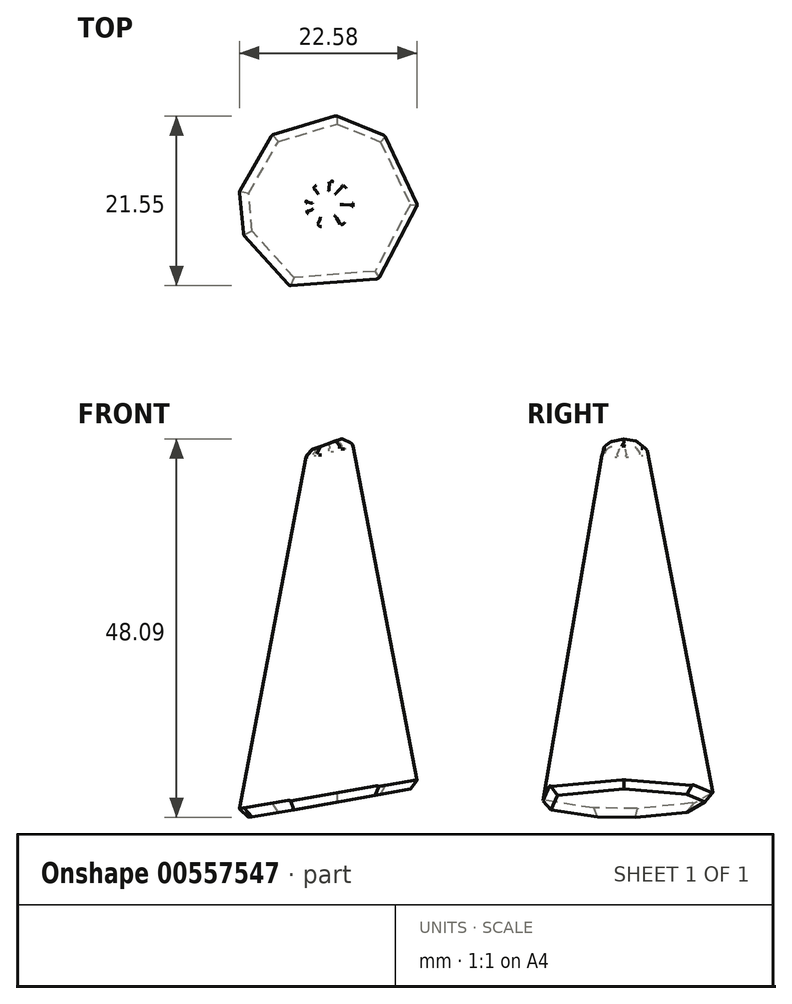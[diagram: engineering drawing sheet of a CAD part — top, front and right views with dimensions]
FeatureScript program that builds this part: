
annotation { "Feature Type Name" : "Feature", "Feature Type Description" : "" }
export const myFeature = defineFeature(function(context is Context, id is Id, definition is map)
    precondition{}
    {
        {
            var Q0;
            Q0=qCreatedBy(makeId("Top.planeOp"),FACE);
            cPlane(context, id + "F0", {"entities" : qUnion([Q0]), "cplaneType" : CPlaneType.OFFSET, "offset" : 60 * mm, "width" : 150 * mm, "height" : 150 * mm});
        }
        {
            var Q0;
            Q0=qCreatedBy(makeId("Top.planeOp"),FACE);
            var sketch = newSketch(context, id + "F1", { "sketchPlane" : qUnion([Q0])});
            skCircle(sketch, "E0", {"center": v(0, 0) * mm, "radius": 12 * mm, "construction": true});
            skLineSegment(sketch, "E1", {"start": v(-11.88, 1.7) * mm, "end": v(-7.77, 9.15) * mm});
            skLineSegment(sketch, "E2", {"start": v(-7.77, 9.15) * mm, "end": v(0.67, 11.98) * mm});
            skLineSegment(sketch, "E3", {"start": v(0.67, 11.98) * mm, "end": v(7.4, 9.44) * mm});
            skLineSegment(sketch, "E4", {"start": v(7.4, 9.44) * mm, "end": v(12, 0) * mm});
            skLineSegment(sketch, "E5", {"start": v(12, 0) * mm, "end": v(6.49, -10.1) * mm});
            skLineSegment(sketch, "E6", {"start": v(6.49, -10.1) * mm, "end": v(-5.5, -10.67) * mm});
            skLineSegment(sketch, "E7", {"start": v(-5.5, -10.67) * mm, "end": v(-11.37, -3.85) * mm});
            skLineSegment(sketch, "E8", {"start": v(-11.37, -3.85) * mm, "end": v(-11.88, 1.7) * mm});
            skSolve(sketch);
        }
        {
            var Q0;
            Q0=qCreatedBy(id+"F0.planeOp",FACE);
            var sketch = newSketch(context, id + "F2", { "sketchPlane" : qUnion([Q0])});
            skCircle(sketch, "E9", {"center": v(0, 0) * mm, "radius": 0.5 * mm, "construction": true});
            skPoint(sketch, "E10.0", {"position": v(-7.77, 9.15) * mm});
            skPoint(sketch, "E11.0", {"position": v(0.67, 11.98) * mm});
            skPoint(sketch, "E12.0", {"position": v(7.4, 9.44) * mm});
            skPoint(sketch, "E13.0", {"position": v(12, 0) * mm});
            skPoint(sketch, "E14.0", {"position": v(6.49, -10.1) * mm});
            skPoint(sketch, "E15.0", {"position": v(-5.5, -10.67) * mm});
            skPoint(sketch, "E16.0", {"position": v(-11.37, -3.85) * mm});
            skPoint(sketch, "E17.0", {"position": v(-11.88, 1.7) * mm});
            skLineSegment(sketch, "E18", {"start": v(0, 0) * mm, "end": v(-7.77, 9.15) * mm, "construction": true});
            skLineSegment(sketch, "E19", {"start": v(0, 0) * mm, "end": v(0.67, 11.98) * mm, "construction": true});
            skLineSegment(sketch, "E20", {"start": v(0, 0) * mm, "end": v(7.4, 9.44) * mm, "construction": true});
            skLineSegment(sketch, "E21", {"start": v(0, 0) * mm, "end": v(12, 0) * mm, "construction": true});
            skLineSegment(sketch, "E22", {"start": v(6.49, -10.1) * mm, "end": v(0, 0) * mm, "construction": true});
            skLineSegment(sketch, "E23", {"start": v(-5.5, -10.67) * mm, "end": v(0, 0) * mm, "construction": true});
            skLineSegment(sketch, "E24", {"start": v(-11.37, -3.85) * mm, "end": v(0, 0) * mm, "construction": true});
            skLineSegment(sketch, "E25", {"start": v(-11.88, 1.7) * mm, "end": v(0, 0) * mm, "construction": true});
            skLineSegment(sketch, "E26", {"start": v(0.03, 0.5) * mm, "end": v(0.3, 0.4) * mm});
            skLineSegment(sketch, "E27", {"start": v(0.3, 0.4) * mm, "end": v(0.5, 0) * mm});
            skLineSegment(sketch, "E28", {"start": v(0.5, 0) * mm, "end": v(0.27, -0.42) * mm});
            skLineSegment(sketch, "E29", {"start": v(0.27, -0.42) * mm, "end": v(-0.23, -0.44) * mm});
            skLineSegment(sketch, "E30", {"start": v(-0.23, -0.44) * mm, "end": v(-0.47, -0.16) * mm});
            skLineSegment(sketch, "E31", {"start": v(-0.47, -0.16) * mm, "end": v(-0.5, 0.07) * mm});
            skLineSegment(sketch, "E32", {"start": v(-0.5, 0.07) * mm, "end": v(-0.32, 0.38) * mm});
            skLineSegment(sketch, "E33", {"start": v(-0.32, 0.38) * mm, "end": v(0.03, 0.5) * mm});
            skSolve(sketch);
        }
        {
            var Q0;
            Q0=qSketchRegion(id+"F2",true);
            var Q1;
            Q1=qSketchRegion(id+"F1",true);
            loft(context, id + "F3", {"sheetProfilesArray" : [{ "sheetProfileEntities" : qUnion([Q0]) }, { "sheetProfileEntities" : qUnion([Q1]) }]});
        }
        {
            var Q0;
            Q0=qCreatedBy(makeId("Front.planeOp"),FACE);
            var sketch = newSketch(context, id + "F4", { "sketchPlane" : qUnion([Q0])});
            skLineSegment(sketch, "E34", {"start": v(-11.88, 0) * mm, "end": v(12, 4.21) * mm});
            skLineSegment(sketch, "E35", {"start": v(12, 4.21) * mm, "end": v(12, 0) * mm});
            skLineSegment(sketch, "E36", {"start": v(12, 0) * mm, "end": v(-11.88, 0) * mm});
            skSolve(sketch);
        }
        {
            var Q0;
            Q0=qSketchRegion(id+"F4",true);
            extrude(context, id + "F5", {"entities" : qUnion([Q0]), "operationType" : NewBodyOperationType.REMOVE, "endBound" : BoundingType.THROUGH_ALL, "oppositeDirection" : true, "depth" : 25 * mm, "offsetDistance" : 25 * mm, "hasSecondDirection" : true, "secondDirectionBound" : BoundingType.THROUGH_ALL, "secondDirectionOppositeDirection" : false, "secondDirectionDepth" : 25 * mm});
        }
        {
            var Q0;
            Q0=qCreatedBy(makeId("Front.planeOp"),FACE);
            var sketch = newSketch(context, id + "F6", { "sketchPlane" : qUnion([Q0])});
            skLineSegment(sketch, "E37", {"start": v(-3, 46.8) * mm, "end": v(2.64, 48.85) * mm});
            skLineSegment(sketch, "E38", {"start": v(2.64, 48.85) * mm, "end": v(0.5, 60) * mm});
            skLineSegment(sketch, "E39", {"start": v(0.5, 60) * mm, "end": v(-0.5, 60) * mm});
            skLineSegment(sketch, "E40", {"start": v(-0.5, 60) * mm, "end": v(-3, 46.8) * mm});
            skSolve(sketch);
        }
        {
            var Q0;
            Q0 = qSketchRegion(id + "F6", true);
            extrude(context, id + "F7", {"entities" : qUnion([Q0]), "operationType" : NewBodyOperationType.REMOVE, "endBound" : BoundingType.THROUGH_ALL, "oppositeDirection" : true, "depth" : 25 * mm, "offsetDistance" : 25 * mm, "hasSecondDirection" : true, "secondDirectionBound" : BoundingType.THROUGH_ALL, "secondDirectionOppositeDirection" : false, "secondDirectionDepth" : 25 * mm});
        }
        {
            var Q0;
            Q0=makeQuery(id+"F5.boolean.opBoolean","INTERSECT",EDGE,{"derivedFrom":[makeQuery(id+"F3.opLoft","SWEPT_FACE",FACE,{"disambiguationData":[OSD([sQuery(id+"F1.wireOp",EDGE,"E5"),sQuery(id+"F1.wireOp",EDGE,"E6"),sQuery(id+"F1.wireOp",EDGE,"E7"),sQuery(id+"F2.wireOp",EDGE,"E28"),sQuery(id+"F2.wireOp",EDGE,"E29"),sQuery(id+"F2.wireOp",EDGE,"E30")])]}),makeQuery(id+"F5.opExtrude","SWEPT_FACE",FACE,{"disambiguationData":[OSD([sQuery(id+"F4.wireOp",EDGE,"E34")])]})]});
            var Q1;
            Q1=makeQuery(id+"F5.boolean.opBoolean","INTERSECT",EDGE,{"derivedFrom":[makeQuery(id+"F3.opLoft","SWEPT_FACE",FACE,{"disambiguationData":[OSD([sQuery(id+"F1.wireOp",EDGE,"E4"),sQuery(id+"F1.wireOp",EDGE,"E5"),sQuery(id+"F1.wireOp",EDGE,"E6"),sQuery(id+"F2.wireOp",EDGE,"E27"),sQuery(id+"F2.wireOp",EDGE,"E28"),sQuery(id+"F2.wireOp",EDGE,"E29")])]}),makeQuery(id+"F5.opExtrude","SWEPT_FACE",FACE,{"disambiguationData":[OSD([sQuery(id+"F4.wireOp",EDGE,"E34")])]})]});
            var Q2;
            Q2=makeQuery(id+"F5.boolean.opBoolean","INTERSECT",EDGE,{"derivedFrom":[makeQuery(id+"F3.opLoft","SWEPT_FACE",FACE,{"disambiguationData":[OSD([sQuery(id+"F1.wireOp",EDGE,"E6"),sQuery(id+"F1.wireOp",EDGE,"E7"),sQuery(id+"F1.wireOp",EDGE,"E8"),sQuery(id+"F2.wireOp",EDGE,"E29"),sQuery(id+"F2.wireOp",EDGE,"E30"),sQuery(id+"F2.wireOp",EDGE,"E31")])]}),makeQuery(id+"F5.opExtrude","SWEPT_FACE",FACE,{"disambiguationData":[OSD([sQuery(id+"F4.wireOp",EDGE,"E34")])]})]});
            var Q3;
            Q3=makeQuery(id+"F5.boolean.opBoolean","INTERSECT",EDGE,{"derivedFrom":[makeQuery(id+"F3.opLoft","SWEPT_FACE",FACE,{"disambiguationData":[OSD([sQuery(id+"F1.wireOp",EDGE,"E1"),sQuery(id+"F1.wireOp",EDGE,"E7"),sQuery(id+"F1.wireOp",EDGE,"E8"),sQuery(id+"F2.wireOp",EDGE,"E30"),sQuery(id+"F2.wireOp",EDGE,"E31"),sQuery(id+"F2.wireOp",EDGE,"E32")])]}),makeQuery(id+"F5.opExtrude","SWEPT_FACE",FACE,{"disambiguationData":[OSD([sQuery(id+"F4.wireOp",EDGE,"E34")])]})]});
            var Q4;
            Q4=makeQuery(id+"F5.boolean.opBoolean","INTERSECT",EDGE,{"derivedFrom":[makeQuery(id+"F3.opLoft","SWEPT_FACE",FACE,{"disambiguationData":[OSD([sQuery(id+"F1.wireOp",EDGE,"E3"),sQuery(id+"F1.wireOp",EDGE,"E4"),sQuery(id+"F1.wireOp",EDGE,"E5"),sQuery(id+"F2.wireOp",EDGE,"E26"),sQuery(id+"F2.wireOp",EDGE,"E27"),sQuery(id+"F2.wireOp",EDGE,"E28")])]}),makeQuery(id+"F5.opExtrude","SWEPT_FACE",FACE,{"disambiguationData":[OSD([sQuery(id+"F4.wireOp",EDGE,"E34")])]})]});
            var Q5;
            Q5=makeQuery(id+"F5.boolean.opBoolean","INTERSECT",EDGE,{"derivedFrom":[makeQuery(id+"F3.opLoft","SWEPT_FACE",FACE,{"disambiguationData":[OSD([sQuery(id+"F1.wireOp",EDGE,"E2"),sQuery(id+"F1.wireOp",EDGE,"E3"),sQuery(id+"F1.wireOp",EDGE,"E4"),sQuery(id+"F2.wireOp",EDGE,"E26"),sQuery(id+"F2.wireOp",EDGE,"E27"),sQuery(id+"F2.wireOp",EDGE,"E33")])]}),makeQuery(id+"F5.opExtrude","SWEPT_FACE",FACE,{"disambiguationData":[OSD([sQuery(id+"F4.wireOp",EDGE,"E34")])]})]});
            var Q6;
            Q6=makeQuery(id+"F5.boolean.opBoolean","INTERSECT",EDGE,{"derivedFrom":[makeQuery(id+"F3.opLoft","SWEPT_FACE",FACE,{"disambiguationData":[OSD([sQuery(id+"F1.wireOp",EDGE,"E1"),sQuery(id+"F1.wireOp",EDGE,"E2"),sQuery(id+"F1.wireOp",EDGE,"E3"),sQuery(id+"F2.wireOp",EDGE,"E26"),sQuery(id+"F2.wireOp",EDGE,"E32"),sQuery(id+"F2.wireOp",EDGE,"E33")])]}),makeQuery(id+"F5.opExtrude","SWEPT_FACE",FACE,{"disambiguationData":[OSD([sQuery(id+"F4.wireOp",EDGE,"E34")])]})]});
            var Q7;
            Q7=makeQuery(id+"F5.boolean.opBoolean","INTERSECT",EDGE,{"derivedFrom":[makeQuery(id+"F3.opLoft","SWEPT_FACE",FACE,{"disambiguationData":[OSD([sQuery(id+"F1.wireOp",EDGE,"E1"),sQuery(id+"F1.wireOp",EDGE,"E2"),sQuery(id+"F1.wireOp",EDGE,"E8"),sQuery(id+"F2.wireOp",EDGE,"E31"),sQuery(id+"F2.wireOp",EDGE,"E32"),sQuery(id+"F2.wireOp",EDGE,"E33")])]}),makeQuery(id+"F5.opExtrude","SWEPT_FACE",FACE,{"disambiguationData":[OSD([sQuery(id+"F4.wireOp",EDGE,"E34")])]})]});
            chamfer(context, id + "F8", {"entities" : qUnion([Q0, Q1, Q2, Q3, Q4, Q5, Q6, Q7]), "width" : 1 * mm, "tangentPropagation" : true});
        }
        {
            var Q0;
            Q0=makeQuery(id+"F7.boolean.opBoolean","COPY",FACE,{"derivedFrom":makeQuery(id+"F7.opExtrude","SWEPT_FACE",FACE,{"disambiguationData":[OSD([sQuery(id+"F6.wireOp",EDGE,"E37")])]})});
            chamfer(context, id + "F9", {"entities" : qUnion([Q0]), "width" : 1 * mm, "tangentPropagation" : true});
        }
        {
            var Q0;
            Q0=makeQuery(id+"F3.opLoft","SWEPT_EDGE",EDGE,{"disambiguationData":[OSD([sQuery(id+"F1.wireOp",EDGE,"E5"),sQuery(id+"F1.wireOp",EDGE,"E6"),sQuery(id+"F2.wireOp",EDGE,"E28"),sQuery(id+"F2.wireOp",EDGE,"E29")])]});
            var Q1;
            Q1=makeQuery(id+"F3.opLoft","SWEPT_EDGE",EDGE,{"disambiguationData":[OSD([sQuery(id+"F1.wireOp",EDGE,"E6"),sQuery(id+"F1.wireOp",EDGE,"E7"),sQuery(id+"F2.wireOp",EDGE,"E29"),sQuery(id+"F2.wireOp",EDGE,"E30")])]});
            var Q2;
            Q2=makeQuery(id+"F3.opLoft","SWEPT_EDGE",EDGE,{"disambiguationData":[OSD([sQuery(id+"F1.wireOp",EDGE,"E4"),sQuery(id+"F1.wireOp",EDGE,"E5"),sQuery(id+"F2.wireOp",EDGE,"E27"),sQuery(id+"F2.wireOp",EDGE,"E28")])]});
            var Q3;
            Q3=makeQuery(id+"F3.opLoft","SWEPT_EDGE",EDGE,{"disambiguationData":[OSD([sQuery(id+"F1.wireOp",EDGE,"E3"),sQuery(id+"F1.wireOp",EDGE,"E4"),sQuery(id+"F2.wireOp",EDGE,"E26"),sQuery(id+"F2.wireOp",EDGE,"E27")])]});
            var Q4;
            Q4=makeQuery(id+"F3.opLoft","SWEPT_EDGE",EDGE,{"disambiguationData":[OSD([sQuery(id+"F1.wireOp",EDGE,"E2"),sQuery(id+"F1.wireOp",EDGE,"E3"),sQuery(id+"F2.wireOp",EDGE,"E26"),sQuery(id+"F2.wireOp",EDGE,"E33")])]});
            var Q5;
            Q5=makeQuery(id+"F3.opLoft","SWEPT_EDGE",EDGE,{"disambiguationData":[OSD([sQuery(id+"F1.wireOp",EDGE,"E7"),sQuery(id+"F1.wireOp",EDGE,"E8"),sQuery(id+"F2.wireOp",EDGE,"E30"),sQuery(id+"F2.wireOp",EDGE,"E31")])]});
            var Q6;
            Q6=makeQuery(id+"F3.opLoft","SWEPT_EDGE",EDGE,{"disambiguationData":[OSD([sQuery(id+"F1.wireOp",EDGE,"E1"),sQuery(id+"F1.wireOp",EDGE,"E8"),sQuery(id+"F2.wireOp",EDGE,"E31"),sQuery(id+"F2.wireOp",EDGE,"E32")])]});
            var Q7;
            Q7=makeQuery(id+"F3.opLoft","SWEPT_EDGE",EDGE,{"disambiguationData":[OSD([sQuery(id+"F1.wireOp",EDGE,"E1"),sQuery(id+"F1.wireOp",EDGE,"E2"),sQuery(id+"F2.wireOp",EDGE,"E32"),sQuery(id+"F2.wireOp",EDGE,"E33")])]});
            fillet(context, id + "F10", {"entities" : qUnion([Q0, Q1, Q2, Q3, Q4, Q5, Q6, Q7]), "radius" : 0.5 * mm, "tangentPropagation" : true, "allowEdgeOverflow" : false});
        }
        {
            var Q0;
            {var subQ0=makeQuery(id+"F3.opLoft","SWEPT_FACE",FACE,{"disambiguationData":[OSD([sQuery(id+"F1.wireOp",EDGE,"E6"),sQuery(id+"F1.wireOp",EDGE,"E7"),sQuery(id+"F1.wireOp",EDGE,"E8"),sQuery(id+"F2.wireOp",EDGE,"E29"),sQuery(id+"F2.wireOp",EDGE,"E30"),sQuery(id+"F2.wireOp",EDGE,"E31")])]});Q0=makeQuery(id+"F9.opChamfer","BLEND_EDGE",EDGE,{"blendedFrom":[makeQuery(id+"F7.boolean.opBoolean","INTERSECT",EDGE,{"derivedFrom":[subQ0,makeQuery(id+"F7.opExtrude","SWEPT_FACE",FACE,{"disambiguationData":[OSD([sQuery(id+"F6.wireOp",EDGE,"E37")])]})]}),subQ0],"blendedInto":[subQ0]});}
            var Q1;
            {var subQ0=makeQuery(id+"F3.opLoft","SWEPT_FACE",FACE,{"disambiguationData":[OSD([sQuery(id+"F1.wireOp",EDGE,"E5"),sQuery(id+"F1.wireOp",EDGE,"E6"),sQuery(id+"F1.wireOp",EDGE,"E7"),sQuery(id+"F2.wireOp",EDGE,"E28"),sQuery(id+"F2.wireOp",EDGE,"E29"),sQuery(id+"F2.wireOp",EDGE,"E30")])]});Q1=makeQuery(id+"F9.opChamfer","BLEND_EDGE",EDGE,{"blendedFrom":[makeQuery(id+"F7.boolean.opBoolean","INTERSECT",EDGE,{"derivedFrom":[subQ0,makeQuery(id+"F7.opExtrude","SWEPT_FACE",FACE,{"disambiguationData":[OSD([sQuery(id+"F6.wireOp",EDGE,"E37")])]})]}),subQ0],"blendedInto":[subQ0]});}
            var Q2;
            {var subQ0=makeQuery(id+"F3.opLoft","SWEPT_FACE",FACE,{"disambiguationData":[OSD([sQuery(id+"F1.wireOp",EDGE,"E4"),sQuery(id+"F1.wireOp",EDGE,"E5"),sQuery(id+"F1.wireOp",EDGE,"E6"),sQuery(id+"F2.wireOp",EDGE,"E27"),sQuery(id+"F2.wireOp",EDGE,"E28"),sQuery(id+"F2.wireOp",EDGE,"E29")])]});Q2=makeQuery(id+"F9.opChamfer","BLEND_EDGE",EDGE,{"blendedFrom":[makeQuery(id+"F7.boolean.opBoolean","INTERSECT",EDGE,{"derivedFrom":[subQ0,makeQuery(id+"F7.opExtrude","SWEPT_FACE",FACE,{"disambiguationData":[OSD([sQuery(id+"F6.wireOp",EDGE,"E37")])]})]}),subQ0],"blendedInto":[subQ0]});}
            var Q3;
            {var subQ0=makeQuery(id+"F3.opLoft","SWEPT_FACE",FACE,{"disambiguationData":[OSD([sQuery(id+"F1.wireOp",EDGE,"E3"),sQuery(id+"F1.wireOp",EDGE,"E4"),sQuery(id+"F1.wireOp",EDGE,"E5"),sQuery(id+"F2.wireOp",EDGE,"E26"),sQuery(id+"F2.wireOp",EDGE,"E27"),sQuery(id+"F2.wireOp",EDGE,"E28")])]});Q3=makeQuery(id+"F9.opChamfer","BLEND_EDGE",EDGE,{"blendedFrom":[makeQuery(id+"F7.boolean.opBoolean","INTERSECT",EDGE,{"derivedFrom":[subQ0,makeQuery(id+"F7.opExtrude","SWEPT_FACE",FACE,{"disambiguationData":[OSD([sQuery(id+"F6.wireOp",EDGE,"E37")])]})]}),subQ0],"blendedInto":[subQ0]});}
            var Q4;
            {var subQ0=makeQuery(id+"F3.opLoft","SWEPT_FACE",FACE,{"disambiguationData":[OSD([sQuery(id+"F1.wireOp",EDGE,"E2"),sQuery(id+"F1.wireOp",EDGE,"E3"),sQuery(id+"F1.wireOp",EDGE,"E4"),sQuery(id+"F2.wireOp",EDGE,"E26"),sQuery(id+"F2.wireOp",EDGE,"E27"),sQuery(id+"F2.wireOp",EDGE,"E33")])]});Q4=makeQuery(id+"F9.opChamfer","BLEND_EDGE",EDGE,{"blendedFrom":[makeQuery(id+"F7.boolean.opBoolean","INTERSECT",EDGE,{"derivedFrom":[subQ0,makeQuery(id+"F7.opExtrude","SWEPT_FACE",FACE,{"disambiguationData":[OSD([sQuery(id+"F6.wireOp",EDGE,"E37")])]})]}),subQ0],"blendedInto":[subQ0]});}
            var Q5;
            {var subQ0=makeQuery(id+"F3.opLoft","SWEPT_FACE",FACE,{"disambiguationData":[OSD([sQuery(id+"F1.wireOp",EDGE,"E1"),sQuery(id+"F1.wireOp",EDGE,"E2"),sQuery(id+"F1.wireOp",EDGE,"E3"),sQuery(id+"F2.wireOp",EDGE,"E26"),sQuery(id+"F2.wireOp",EDGE,"E32"),sQuery(id+"F2.wireOp",EDGE,"E33")])]});Q5=makeQuery(id+"F9.opChamfer","BLEND_EDGE",EDGE,{"blendedFrom":[makeQuery(id+"F7.boolean.opBoolean","INTERSECT",EDGE,{"derivedFrom":[subQ0,makeQuery(id+"F7.opExtrude","SWEPT_FACE",FACE,{"disambiguationData":[OSD([sQuery(id+"F6.wireOp",EDGE,"E37")])]})]}),subQ0],"blendedInto":[subQ0]});}
            var Q6;
            {var subQ0=makeQuery(id+"F3.opLoft","SWEPT_FACE",FACE,{"disambiguationData":[OSD([sQuery(id+"F1.wireOp",EDGE,"E1"),sQuery(id+"F1.wireOp",EDGE,"E2"),sQuery(id+"F1.wireOp",EDGE,"E8"),sQuery(id+"F2.wireOp",EDGE,"E31"),sQuery(id+"F2.wireOp",EDGE,"E32"),sQuery(id+"F2.wireOp",EDGE,"E33")])]});Q6=makeQuery(id+"F9.opChamfer","BLEND_EDGE",EDGE,{"blendedFrom":[makeQuery(id+"F7.boolean.opBoolean","INTERSECT",EDGE,{"derivedFrom":[subQ0,makeQuery(id+"F7.opExtrude","SWEPT_FACE",FACE,{"disambiguationData":[OSD([sQuery(id+"F6.wireOp",EDGE,"E37")])]})]}),subQ0],"blendedInto":[subQ0]});}
            var Q7;
            {var subQ0=makeQuery(id+"F3.opLoft","SWEPT_FACE",FACE,{"disambiguationData":[OSD([sQuery(id+"F1.wireOp",EDGE,"E1"),sQuery(id+"F1.wireOp",EDGE,"E7"),sQuery(id+"F1.wireOp",EDGE,"E8"),sQuery(id+"F2.wireOp",EDGE,"E30"),sQuery(id+"F2.wireOp",EDGE,"E31"),sQuery(id+"F2.wireOp",EDGE,"E32")])]});Q7=makeQuery(id+"F9.opChamfer","BLEND_EDGE",EDGE,{"blendedFrom":[makeQuery(id+"F7.boolean.opBoolean","INTERSECT",EDGE,{"derivedFrom":[subQ0,makeQuery(id+"F7.opExtrude","SWEPT_FACE",FACE,{"disambiguationData":[OSD([sQuery(id+"F6.wireOp",EDGE,"E37")])]})]}),subQ0],"blendedInto":[subQ0]});}
            var Q8;
            {var subQ0=makeQuery(id+"F7.opExtrude","SWEPT_FACE",FACE,{"disambiguationData":[OSD([sQuery(id+"F6.wireOp",EDGE,"E37")])]});Q8=makeQuery(id+"F9.opChamfer","BLEND_EDGE",EDGE,{"blendedFrom":[makeQuery(id+"F7.boolean.opBoolean","INTERSECT",EDGE,{"derivedFrom":[makeQuery(id+"F3.opLoft","SWEPT_FACE",FACE,{"disambiguationData":[OSD([sQuery(id+"F1.wireOp",EDGE,"E6"),sQuery(id+"F1.wireOp",EDGE,"E7"),sQuery(id+"F1.wireOp",EDGE,"E8"),sQuery(id+"F2.wireOp",EDGE,"E29"),sQuery(id+"F2.wireOp",EDGE,"E30"),sQuery(id+"F2.wireOp",EDGE,"E31")])]}),subQ0]}),makeQuery(id+"F7.boolean.opBoolean","COPY",FACE,{"derivedFrom":subQ0})],"blendedInto":[makeQuery(id+"F7.boolean.opBoolean","COPY",FACE,{"derivedFrom":subQ0})]});}
            var Q9;
            {var subQ0=makeQuery(id+"F7.opExtrude","SWEPT_FACE",FACE,{"disambiguationData":[OSD([sQuery(id+"F6.wireOp",EDGE,"E37")])]});Q9=makeQuery(id+"F9.opChamfer","BLEND_EDGE",EDGE,{"blendedFrom":[makeQuery(id+"F7.boolean.opBoolean","INTERSECT",EDGE,{"derivedFrom":[makeQuery(id+"F3.opLoft","SWEPT_FACE",FACE,{"disambiguationData":[OSD([sQuery(id+"F1.wireOp",EDGE,"E1"),sQuery(id+"F1.wireOp",EDGE,"E7"),sQuery(id+"F1.wireOp",EDGE,"E8"),sQuery(id+"F2.wireOp",EDGE,"E30"),sQuery(id+"F2.wireOp",EDGE,"E31"),sQuery(id+"F2.wireOp",EDGE,"E32")])]}),subQ0]}),makeQuery(id+"F7.boolean.opBoolean","COPY",FACE,{"derivedFrom":subQ0})],"blendedInto":[makeQuery(id+"F7.boolean.opBoolean","COPY",FACE,{"derivedFrom":subQ0})]});}
            var Q10;
            {var subQ0=makeQuery(id+"F7.opExtrude","SWEPT_FACE",FACE,{"disambiguationData":[OSD([sQuery(id+"F6.wireOp",EDGE,"E37")])]});Q10=makeQuery(id+"F9.opChamfer","BLEND_EDGE",EDGE,{"blendedFrom":[makeQuery(id+"F7.boolean.opBoolean","INTERSECT",EDGE,{"derivedFrom":[makeQuery(id+"F3.opLoft","SWEPT_FACE",FACE,{"disambiguationData":[OSD([sQuery(id+"F1.wireOp",EDGE,"E1"),sQuery(id+"F1.wireOp",EDGE,"E2"),sQuery(id+"F1.wireOp",EDGE,"E8"),sQuery(id+"F2.wireOp",EDGE,"E31"),sQuery(id+"F2.wireOp",EDGE,"E32"),sQuery(id+"F2.wireOp",EDGE,"E33")])]}),subQ0]}),makeQuery(id+"F7.boolean.opBoolean","COPY",FACE,{"derivedFrom":subQ0})],"blendedInto":[makeQuery(id+"F7.boolean.opBoolean","COPY",FACE,{"derivedFrom":subQ0})]});}
            var Q11;
            {var subQ0=makeQuery(id+"F7.opExtrude","SWEPT_FACE",FACE,{"disambiguationData":[OSD([sQuery(id+"F6.wireOp",EDGE,"E37")])]});Q11=makeQuery(id+"F9.opChamfer","BLEND_EDGE",EDGE,{"blendedFrom":[makeQuery(id+"F7.boolean.opBoolean","INTERSECT",EDGE,{"derivedFrom":[makeQuery(id+"F3.opLoft","SWEPT_FACE",FACE,{"disambiguationData":[OSD([sQuery(id+"F1.wireOp",EDGE,"E1"),sQuery(id+"F1.wireOp",EDGE,"E2"),sQuery(id+"F1.wireOp",EDGE,"E3"),sQuery(id+"F2.wireOp",EDGE,"E26"),sQuery(id+"F2.wireOp",EDGE,"E32"),sQuery(id+"F2.wireOp",EDGE,"E33")])]}),subQ0]}),makeQuery(id+"F7.boolean.opBoolean","COPY",FACE,{"derivedFrom":subQ0})],"blendedInto":[makeQuery(id+"F7.boolean.opBoolean","COPY",FACE,{"derivedFrom":subQ0})]});}
            var Q12;
            {var subQ0=makeQuery(id+"F7.opExtrude","SWEPT_FACE",FACE,{"disambiguationData":[OSD([sQuery(id+"F6.wireOp",EDGE,"E37")])]});Q12=makeQuery(id+"F9.opChamfer","BLEND_EDGE",EDGE,{"blendedFrom":[makeQuery(id+"F7.boolean.opBoolean","INTERSECT",EDGE,{"derivedFrom":[makeQuery(id+"F3.opLoft","SWEPT_FACE",FACE,{"disambiguationData":[OSD([sQuery(id+"F1.wireOp",EDGE,"E2"),sQuery(id+"F1.wireOp",EDGE,"E3"),sQuery(id+"F1.wireOp",EDGE,"E4"),sQuery(id+"F2.wireOp",EDGE,"E26"),sQuery(id+"F2.wireOp",EDGE,"E27"),sQuery(id+"F2.wireOp",EDGE,"E33")])]}),subQ0]}),makeQuery(id+"F7.boolean.opBoolean","COPY",FACE,{"derivedFrom":subQ0})],"blendedInto":[makeQuery(id+"F7.boolean.opBoolean","COPY",FACE,{"derivedFrom":subQ0})]});}
            var Q13;
            {var subQ0=makeQuery(id+"F7.opExtrude","SWEPT_FACE",FACE,{"disambiguationData":[OSD([sQuery(id+"F6.wireOp",EDGE,"E37")])]});Q13=makeQuery(id+"F9.opChamfer","BLEND_EDGE",EDGE,{"blendedFrom":[makeQuery(id+"F7.boolean.opBoolean","INTERSECT",EDGE,{"derivedFrom":[makeQuery(id+"F3.opLoft","SWEPT_FACE",FACE,{"disambiguationData":[OSD([sQuery(id+"F1.wireOp",EDGE,"E3"),sQuery(id+"F1.wireOp",EDGE,"E4"),sQuery(id+"F1.wireOp",EDGE,"E5"),sQuery(id+"F2.wireOp",EDGE,"E26"),sQuery(id+"F2.wireOp",EDGE,"E27"),sQuery(id+"F2.wireOp",EDGE,"E28")])]}),subQ0]}),makeQuery(id+"F7.boolean.opBoolean","COPY",FACE,{"derivedFrom":subQ0})],"blendedInto":[makeQuery(id+"F7.boolean.opBoolean","COPY",FACE,{"derivedFrom":subQ0})]});}
            var Q14;
            {var subQ0=makeQuery(id+"F7.opExtrude","SWEPT_FACE",FACE,{"disambiguationData":[OSD([sQuery(id+"F6.wireOp",EDGE,"E37")])]});Q14=makeQuery(id+"F9.opChamfer","BLEND_EDGE",EDGE,{"blendedFrom":[makeQuery(id+"F7.boolean.opBoolean","INTERSECT",EDGE,{"derivedFrom":[makeQuery(id+"F3.opLoft","SWEPT_FACE",FACE,{"disambiguationData":[OSD([sQuery(id+"F1.wireOp",EDGE,"E4"),sQuery(id+"F1.wireOp",EDGE,"E5"),sQuery(id+"F1.wireOp",EDGE,"E6"),sQuery(id+"F2.wireOp",EDGE,"E27"),sQuery(id+"F2.wireOp",EDGE,"E28"),sQuery(id+"F2.wireOp",EDGE,"E29")])]}),subQ0]}),makeQuery(id+"F7.boolean.opBoolean","COPY",FACE,{"derivedFrom":subQ0})],"blendedInto":[makeQuery(id+"F7.boolean.opBoolean","COPY",FACE,{"derivedFrom":subQ0})]});}
            var Q15;
            {var subQ0=makeQuery(id+"F7.opExtrude","SWEPT_FACE",FACE,{"disambiguationData":[OSD([sQuery(id+"F6.wireOp",EDGE,"E37")])]});Q15=makeQuery(id+"F9.opChamfer","BLEND_EDGE",EDGE,{"blendedFrom":[makeQuery(id+"F7.boolean.opBoolean","INTERSECT",EDGE,{"derivedFrom":[makeQuery(id+"F3.opLoft","SWEPT_FACE",FACE,{"disambiguationData":[OSD([sQuery(id+"F1.wireOp",EDGE,"E5"),sQuery(id+"F1.wireOp",EDGE,"E6"),sQuery(id+"F1.wireOp",EDGE,"E7"),sQuery(id+"F2.wireOp",EDGE,"E28"),sQuery(id+"F2.wireOp",EDGE,"E29"),sQuery(id+"F2.wireOp",EDGE,"E30")])]}),subQ0]}),makeQuery(id+"F7.boolean.opBoolean","COPY",FACE,{"derivedFrom":subQ0})],"blendedInto":[makeQuery(id+"F7.boolean.opBoolean","COPY",FACE,{"derivedFrom":subQ0})]});}
            fillet(context, id + "F11", {"entities" : qUnion([Q0, Q1, Q2, Q3, Q4, Q5, Q6, Q7, Q8, Q9, Q10, Q11, Q12, Q13, Q14, Q15]), "radius" : 0.5 * mm, "tangentPropagation" : true, "allowEdgeOverflow" : false});
        }
    });
